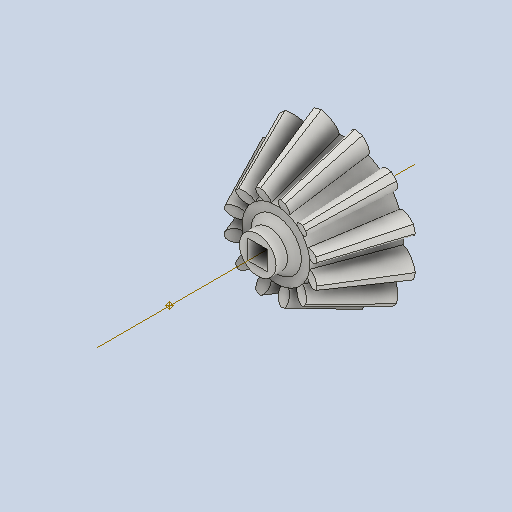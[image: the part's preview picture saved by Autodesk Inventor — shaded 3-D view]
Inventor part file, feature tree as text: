
AUTODESK INVENTOR PART (.ipt)
format: ipt  version: 2022 (Build 260153000, 153)  size: 504,320 bytes
history: native  units: in
note: dims shown in document units (in); Inventor stores cm internally (conversion verified against a paired STEP export)
features: other x30, sketch x3
ambient origin geometry x8: Origin, YZ Plane, XZ Plane, XY Plane, X Axis, Y Axis, Z Axis, Center Point
bodies: Solid1 (feature_tree)
feature tree (33):
  other  "Bevel Gear11_MIR1.ipt"
  other  "Solid1::Bevel Gear11_MIR1.ipt"
  other  "TaggingFeature1"
  other  "Teeth Body Sketch"
  other  "Start Sketch"
  other  "End Sketch"
  other  "End Sketch Right"
  other  "End Sketch Left"
  other  "Body Sketch"
  sketch  "Sketch6"  dims[d0=0.3937in]
  sketch  "Sketch8"  dims[d48=0.0in d49=0.0in d50=90.0deg d52=0.0in d53=0.0in d54=0.0in]
  sketch  "Sketch9"
  other  "3D Sketch Right"
  other  "3D Sketch Left"
  other  "Mesh Plane"
  other  "Top Plane"
  other  "Mesh Plane2"
  other  "Tooth Plane"
  other  "End Plane"
  other  "End Plane Right"
  other  "End Plane Left"
  other  "Z Axis_1"
  other  "Top Point"
  other  "Start Point"
  other  "End Point"
  other  "Srf1"
  other  "Srf1::Derived"
  other  "Start plane iMate"
  other  "Mesh iMate2"
  other  "Axis Angle iMate"
  other  "Axis iMate"
  other  "Mesh iMate"
  other  "Intersection iMate"
